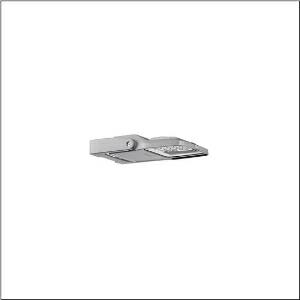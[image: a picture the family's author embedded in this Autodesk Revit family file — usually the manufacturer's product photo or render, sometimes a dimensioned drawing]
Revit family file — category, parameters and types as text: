
# Revit family: floodlight_fl_21_iq_micro___pl52_5xa7762a4d2a_e4f8
name_source: partatom
category: Lighting Fixtures
units: mm (PartAtom-declared; Revit-internal decimal feet)

## family parameters
Cut with Voids When Loaded = No
Host = Face
Light Source = No
Part Type = Normal
Room Calculation Point = No
Round Connector Dimension = Use Diameter
Shared = No

## types (1)
- --- (1 x LED, 3010 lm, 23.1 W, 4000K)
    Apparent Load = 23 VA
    CIE Flux Codes = 26 60 98 100 100
    Color Rendering = 70
    Color Temperature = 4000K
    Default Elevation = 1800 mm
    Description = Floodlight FL 21 iQ micro, floodlight, primary light control with lens, of PMMA, primary optical cover: protective disc, of toughened safety glass, transparent, light distribution: PL52, light emission: direct distribution, installation type: surface-mounted, LED, High Power LED, rated luminous flux: 3.010lm, luminous efficacy: 130lm/W, light colour: 740, colour temperature: 4000K, control gear: iQ Street-Remote/DALI, control: Auto-Match, Temp-Guard, Night-Set, Smart-Wire, Desk-Remote (wireless, voltage-free reading and setting of iQ features in the workshop via application-optimized NFC function/RFID function), optimised constant luminous flux control (CLO 2.0), Street-Remote, with terminal, 6-pole, mains connection: 220..240V, AC, 50/60Hz, start of lifetime: 23W, end of service life: 24W, reduction: 11W, luminaire housing, of diecast aluminium, powder-coated, Siteco® metallic grey (DB 702S), corrosivity category C5 mid according to DIN EN ISO 12944, suitable for swimming pools, chlorine-resistant, sealing non-destructively replaceable, design bracket, of diecast aluminium, powder-coated, Siteco® metallic grey (DB 702S), protection rating (complete): IP66, insulation class (complete): insulation class II (safety insulation), certification: CE, ENEC, VDE, protection symbol: D, impact resistance: IK07, permissible operating ambient temperature: -40..+40°C, permissible operating ambient temperature for outdoor applications: -40..+50°C, standard: DIN EN 12944, LABS conformity tested according to VDMA 24364:2018-05, packaging unit: 1 piece

Light Distribution: PL52
    Height = 65 mm
    Lamp = 1 x LED
    Lamp Light Flux = 3010 lm
    Lamp Power = 23.1 W
    Lamp count = 1
    Length = 312 mm
    Luminous efficacy = 130 lm/W
    Manufacturer = Siteco
    ModVariant = No
    Model = 5XA7762A4D2A
    Mounting Place = Wall
    Mounting Type = Surface mounted
    Number of Poles = 1
    OnlyDefault = Yes
    Power Factor = 1
    Product Name = Floodlight FL 21 iQ micro | PL52
    Product group = floodlight | wall mounted
    ProductGroupID = 2001
    Protection Class = Protection class II
    Protection Degree = IP 66
    RLX_Detail_Level = 1
    RLX_Emergency_Light_Flux = 0 lm
    RLX_Emergency_Type = 0
    RLX_Emergency_Type_DB = No
    RlxData = <blob elided: 97669 chars, md5=49008298>
    Socket = socket
    Standby Power = 0 W
    System Light Flux = 3010 lm
    System Power = 23 W
    Type Comments = factory setting: luminous flux: 100 % | dim-lin: 254 | 455 mA
    Type Image = l_1006878.jpg
    URL = http://relux.com
    VarID = @adj_199243
    Voltage = 0 V
    Weight = 0.00 kg
    Width = 230 mm

## geometry (parser evidence)
native form markers: Blend x4, Sweep x11
no freeform markers — native parametric forms only
